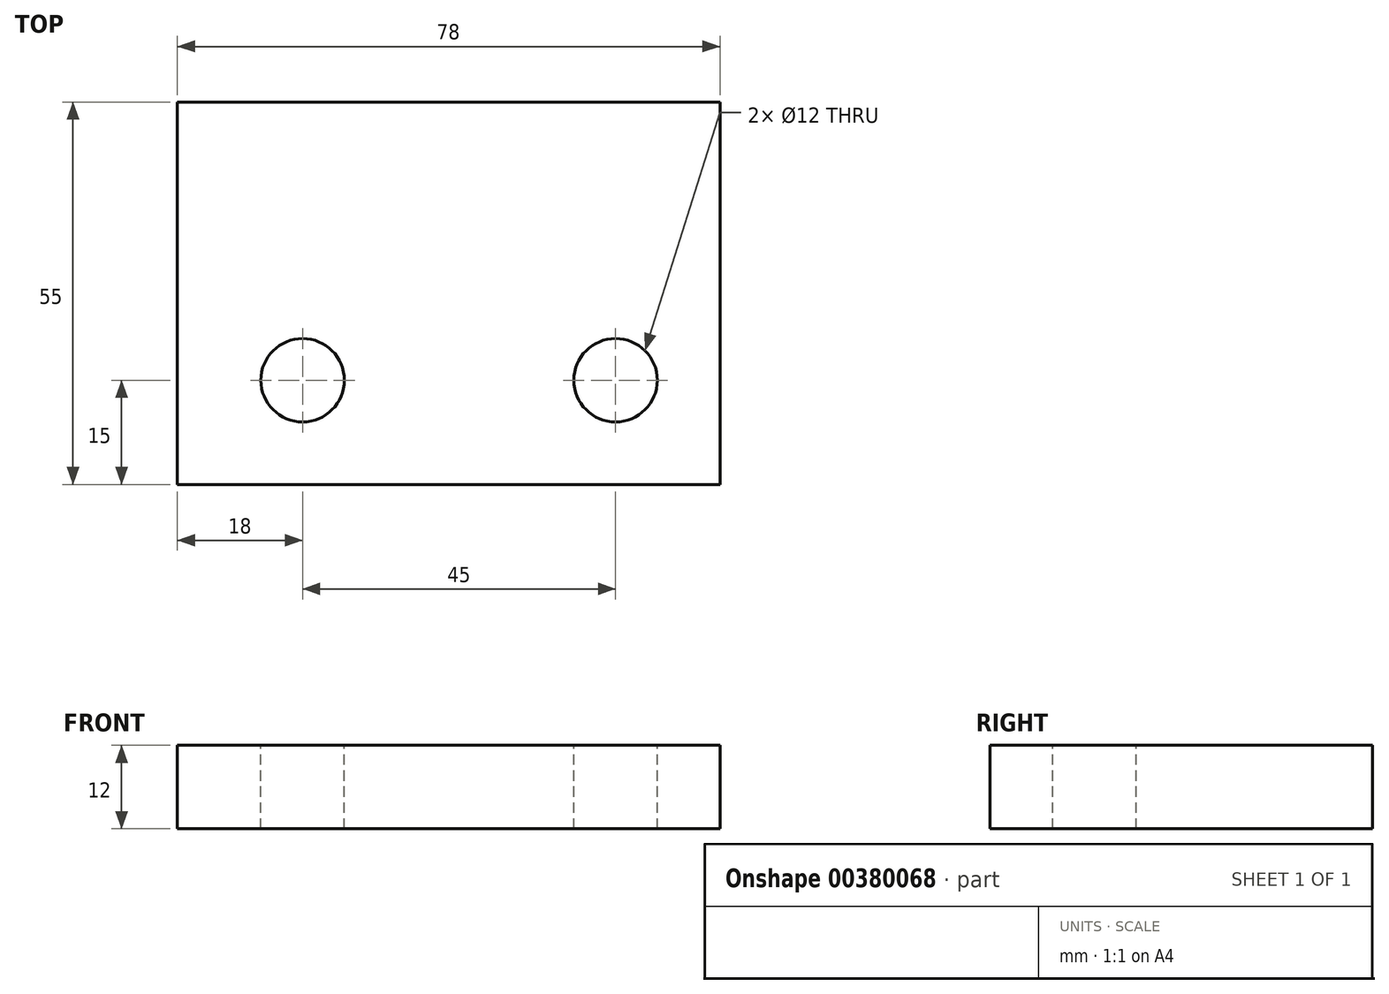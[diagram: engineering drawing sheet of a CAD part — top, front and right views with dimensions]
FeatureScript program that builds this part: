
annotation { "Feature Type Name" : "Feature", "Feature Type Description" : "" }
export const myFeature = defineFeature(function(context is Context, id is Id, definition is map)
    precondition{}
    {
        {
            var Q0;
            Q0=qCreatedBy(makeId("Top.planeOp"),FACE);
            var sketch = newSketch(context, id + "F0", { "sketchPlane" : qUnion([Q0])});
            skLineSegment(sketch, "E0.bottom", {"start": v(0, 0) * mm, "end": v(78, 0) * mm});
            skLineSegment(sketch, "E0.top", {"start": v(0, -55) * mm, "end": v(78, -55) * mm});
            skLineSegment(sketch, "E0.left", {"start": v(0, 0) * mm, "end": v(0, -55) * mm});
            skLineSegment(sketch, "E0.right", {"start": v(78, 0) * mm, "end": v(78, -55) * mm});
            skSolve(sketch);
        }
        {
            var Q0;
            Q0 = qSketchRegion(id + "F0", true);
            extrude(context, id + "F1", {"entities" : qUnion([Q0]), "depth" : 12 * mm});
        }
        {
            var Q0;
            Q0=makeQuery(id+"F1.opExtrude","CAP_FACE",FACE,{"disambiguationData":[OSD([sQuery(id+"F0.wireOp",EDGE,"E0.bottom"),sQuery(id+"F0.wireOp",EDGE,"E0.top"),sQuery(id+"F0.wireOp",EDGE,"E0.left"),sQuery(id+"F0.wireOp",EDGE,"E0.right")])],"isStart":false});
            var sketch = newSketch(context, id + "F2", { "sketchPlane" : qUnion([Q0])});
            skLineSegment(sketch, "E1", {"start": v(78, -55) * mm, "end": v(78, -40) * mm, "construction": true});
            skLineSegment(sketch, "E2", {"start": v(78, -40) * mm, "end": v(63, -40) * mm, "construction": true});
            skLineSegment(sketch, "E3", {"start": v(63, -40) * mm, "end": v(18, -40) * mm, "construction": true});
            skSolve(sketch);
        }
        {
            var Q0;
            Q0=sQuery(id+"F2.wireOp",VERTEX,"E3.end");
            var Q1;
            Q1=sQuery(id+"F2.wireOp",VERTEX,"E3.start");
            var Q2;
            Q2=makeQuery(id+"F1.opExtrude","SWEPT_BODY",BODY,{"disambiguationData":[OSD([sQuery(id+"F0.wireOp",EDGE,"E0.bottom"),sQuery(id+"F0.wireOp",EDGE,"E0.top"),sQuery(id+"F0.wireOp",EDGE,"E0.left"),sQuery(id+"F0.wireOp",EDGE,"E0.right")])]});
            hole(context, id + "F3", {"style" : HoleStyle.SIMPLE, "endStyle" : HoleEndStyle.BLIND, "holeDiameter" : 12 * mm, "holeDepth" : 12 * mm, "isTappedThrough" : true, "tappedDepth" : 12 * mm, "tapClearance" : 3, "locations" : qUnion([Q0, Q1]), "scope" : qUnion([Q2])});
        }
    });
